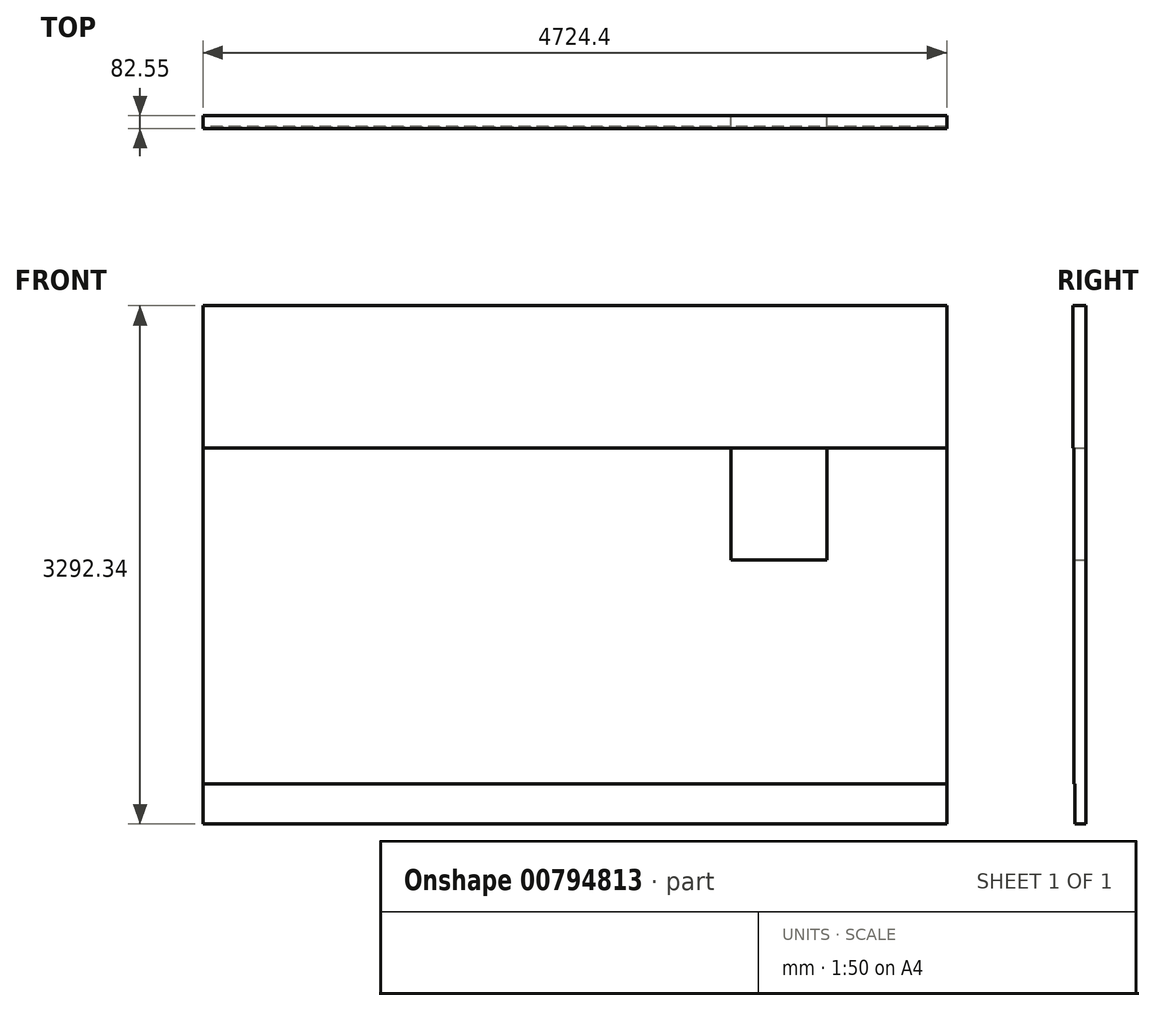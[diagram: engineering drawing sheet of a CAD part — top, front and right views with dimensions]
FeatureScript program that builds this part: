
annotation { "Feature Type Name" : "Feature", "Feature Type Description" : "" }
export const myFeature = defineFeature(function(context is Context, id is Id, definition is map)
    precondition{}
    {
        {
            var Q0;
            Q0=qCreatedBy(makeId("Front.planeOp"),FACE);
            var sketch = newSketch(context, id + "F0", { "sketchPlane" : qUnion([Q0])});
            skLineSegment(sketch, "E0.bottom", {"start": v(-669.15, -683.84) * mm, "end": v(-59.55, -683.84) * mm});
            skLineSegment(sketch, "E0.top", {"start": v(-669.15, -1395.04) * mm, "end": v(-59.55, -1395.04) * mm});
            skLineSegment(sketch, "E0.left", {"start": v(-669.15, -683.84) * mm, "end": v(-669.15, -1395.04) * mm});
            skLineSegment(sketch, "E0.right", {"start": v(-59.55, -683.84) * mm, "end": v(-59.55, -1395.04) * mm});
            skLineSegment(sketch, "E1.bottom", {"start": v(702.45, -683.84) * mm, "end": v(-4021.95, -683.84) * mm});
            skLineSegment(sketch, "E1.top", {"start": v(702.45, -2817.44) * mm, "end": v(-4021.95, -2817.44) * mm});
            skLineSegment(sketch, "E1.left", {"start": v(702.45, -683.84) * mm, "end": v(702.45, -2817.44) * mm});
            skLineSegment(sketch, "E1.right", {"start": v(-4021.95, -683.84) * mm, "end": v(-4021.95, -2817.44) * mm});
            skLineSegment(sketch, "E2.bottom", {"start": v(-4021.95, -2817.44) * mm, "end": v(702.45, -2817.44) * mm});
            skLineSegment(sketch, "E2.top", {"start": v(-4021.95, -3071.44) * mm, "end": v(702.45, -3071.44) * mm});
            skLineSegment(sketch, "E2.left", {"start": v(-4021.95, -2817.44) * mm, "end": v(-4021.95, -3071.44) * mm});
            skLineSegment(sketch, "E2.right", {"start": v(702.45, -2817.44) * mm, "end": v(702.45, -3071.44) * mm});
            skLineSegment(sketch, "E3.bottom", {"start": v(-4021.95, -683.84) * mm, "end": v(702.45, -683.84) * mm});
            skLineSegment(sketch, "E3.top", {"start": v(-4021.95, 220.9) * mm, "end": v(702.45, 220.9) * mm});
            skLineSegment(sketch, "E3.left", {"start": v(-4021.95, -683.84) * mm, "end": v(-4021.95, 220.9) * mm});
            skLineSegment(sketch, "E3.right", {"start": v(702.45, -683.84) * mm, "end": v(702.45, 220.9) * mm});
            skSolve(sketch);
        }
        {
            var Q0;
            {var subQ1=sQuery(id+"F0.wireOp",EDGE,"E0.bottom");Q0=makeQuery(id+"F0.imprint","IMPRINT",FACE,{"disambiguationData":[TD([[makeQuery(id+"F0.imprint","IMPRINT",EDGE,{"derivedFrom":subQ1}),1.0]])]});}
            extrude(context, id + "F1", {"entities" : qUnion([Q0]), "depth" : 82.55 * mm, "offsetDistance" : 25.4 * mm});
        }
        {
            var Q0;
            Q0=makeQuery(id+"F0.imprint","IMPRINT",FACE,{"disambiguationData":[TD([[makeQuery(id+"F0.imprint","IMPRINT",EDGE,{"derivedFrom":sQuery(id+"F0.wireOp",EDGE,"E0.top")}),-1.0]])]});
            extrude(context, id + "F2", {"entities" : qUnion([Q0]), "operationType" : NewBodyOperationType.ADD, "depth" : 76.2 * mm, "offsetDistance" : 25.4 * mm});
        }
        {
            var Q0;
            Q0=makeQuery(id+"F0.imprint","IMPRINT",FACE,{"disambiguationData":[TD([[makeQuery(id+"F0.imprint","IMPRINT",EDGE,{"derivedFrom":sQuery(id+"F0.wireOp",EDGE,"E1.top")}),1.0]])]});
            extrude(context, id + "F3", {"entities" : qUnion([Q0]), "operationType" : NewBodyOperationType.ADD, "depth" : 69.85 * mm, "offsetDistance" : 25.4 * mm});
        }
    });
